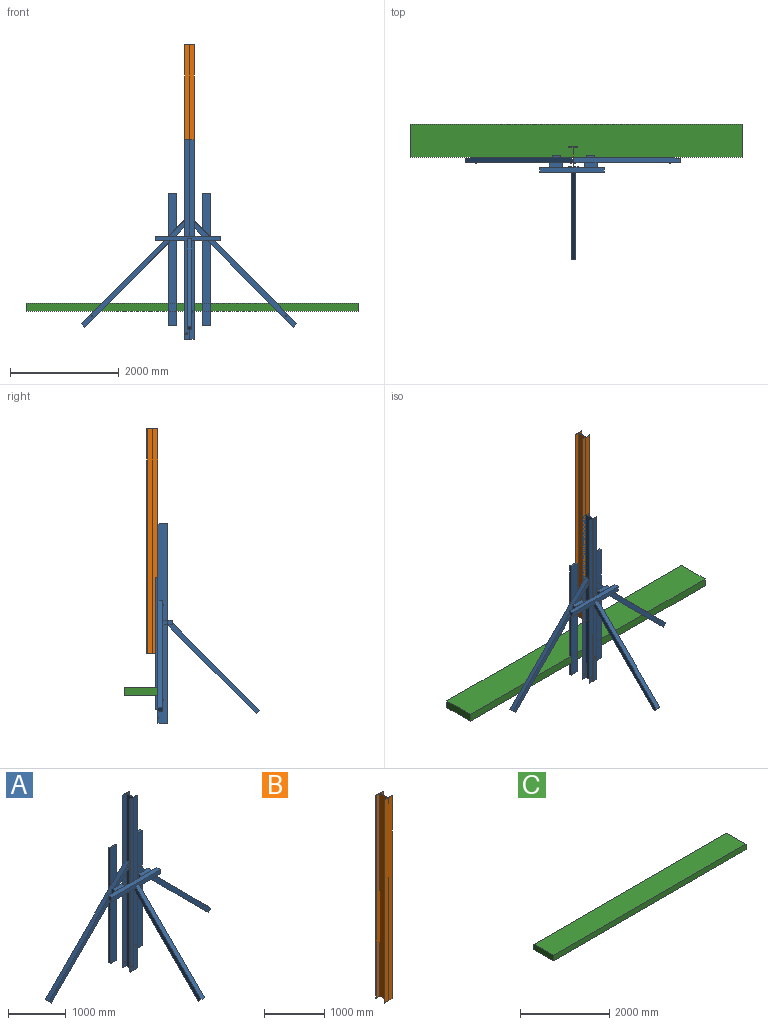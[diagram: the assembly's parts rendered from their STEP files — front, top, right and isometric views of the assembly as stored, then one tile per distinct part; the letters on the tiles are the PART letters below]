
ASSEMBLY  parts=3 mates=2
PART A: 120 faces, bbox 3962x1906.1x3657.6 mm
  f0: plane 1637.43x1605.83mm, normal (0,-1,0), area 194583.3mm2, adj f1,f43,f44,f46,f47,f48,f49,f50
  f1: plane 1915.68x1902.73mm, normal (-0.71,0,-0.7), area 239755.5mm2, adj f0,f7,f9,f11,f42,f43,f45,f80
  f2: plane 1915.68x1902.73mm, normal (0.71,0,-0.7), area 239755.5mm2, adj f3,f6,f8,f60,f61,f63,f64,f87
  f3: plane 1637.43x1617.29mm, normal (0,-1,0), area 194885.1mm2, adj f2,f61,f62,f65,f66,f67,f68,f69
  f4: plane 1766.83x174.77mm, normal (0,-1,0), area 308788mm2, adj f18,f19,f20,f102
  f5: plane 1801.87x174.77mm, normal (0,-1,0), area 313328.6mm2, adj f18,f19,f21,f22,f23,f95,f101,f103
  f6: plane 1671.48x1597.96mm, normal (0,1,0), area 197607.4mm2, adj f2,f61,f62,f88
  f7: plane 276.21x149.05mm, normal (0,1,0), area 18802.6mm2, adj f1,f13,f44,f83
  f8: plane 3657.6x81.77mm, normal (0,-1,0), area 290357mm2, adj f2,f15,f16,f20,f21,f27,f28,f29
  f9: plane 2133.6x77.79mm, normal (0,-1,0), area 162607.1mm2, adj f1,f11,f13,f21,f35,f36,f37,f38
  f10: plane 3657.6x77.79mm, normal (0,1,0), area 283723.8mm2, adj f11,f19,f20,f21,f23
  f11: plane 3657.6x167.29mm, normal (1,0,0), area 600656mm2, adj f1,f9,f10,f12,f20,f21,f42,f44
  f12: plane 1476.16x77.79mm, normal (0,-1,0), area 111781.1mm2, adj f11,f13,f20,f44
  f13: plane 3657.6x9.53mm, normal (1,0,0), area 34838.6mm2, adj f7,f9,f12,f14,f20,f21
  f14: plane 3657.6x174.77mm, normal (0,1,0), area 638983.7mm2, adj f13,f15,f20,f21,f24,f25
  f15: plane 3657.6x9.53mm, normal (-1,0,0), area 34838.6mm2, adj f8,f14,f20,f21,f60
  f16: plane 3657.6x167.29mm, normal (-1,0,0), area 611871mm2, adj f8,f17,f20,f21
  f17: plane 3657.6x81.77mm, normal (0,1,0), area 298275mm2, adj f16,f18,f20,f21,f22
  f18: plane 3657.6x9.53mm, normal (-1,0,0), area 34838.6mm2, adj f4,f5,f17,f20,f21,f98
  f19: plane 3657.6x9.53mm, normal (1,0,0), area 34838.6mm2, adj f4,f5,f10,f20,f21,f99
  f20: plane 186.34x174.77mm, normal (0,0,1), area 5874.8mm2, adj f4,f8,f10,f11,f12,f13,f14,f15
  f21: plane 186.34x174.77mm, normal (0,0,-1), area 5874.8mm2, adj f5,f8,f9,f10,f11,f13,f14,f15
  f22: cylinder r=15.88mm len=31.75mm, axis (0,-1,0), area 950.1mm2, adj f5,f17
  f23: cylinder r=15.88mm len=31.75mm, axis (0,-1,0), area 950.1mm2, adj f5,f10
  f24: cylinder r=6.35mm len=12.7mm, axis (0,-1,0), area 380mm2, adj f14,f41
  f25: cylinder r=6.35mm len=12.7mm, axis (0,-1,0), area 380mm2, adj f14,f33
  f26: plane 22x19.05mm, normal (0,-1,0), area 314.3mm2, adj f27,f28,f29,f30,f31,f32
  f27: plane 12.7x9.53mm, normal (0.87,0,-0.5), area 139.7mm2, adj f8,f26,f28,f32
  f28: plane 12.7x11mm, normal (0,0,-1), area 139.7mm2, adj f8,f26,f27,f29
  f29: plane 12.7x9.52mm, normal (-0.87,0,-0.5), area 139.7mm2, adj f8,f26,f28,f30
  f30: plane 12.7x9.53mm, normal (-0.87,0,0.5), area 139.7mm2, adj f8,f26,f29,f31
  f31: plane 12.7x11mm, normal (0,0,1), area 139.7mm2, adj f8,f26,f30,f32
  f32: plane 12.7x9.52mm, normal (0.87,0,0.5), area 139.7mm2, adj f8,f26,f27,f31
  f33: plane 12.7x12.7mm, normal (0,1,0), area 126.7mm2, adj f25
  f34: plane 21.99x19.26mm, normal (0,-1,0), area 314.3mm2, adj f35,f36,f37,f38,f39,f40
  f35: plane 12.7x9.63mm, normal (0.88,0,-0.48), area 139.7mm2, adj f9,f34,f36,f40
  f36: plane 12.7x11mm, normal (0.02,0,-1), area 139.7mm2, adj f9,f34,f35,f37
  f37: plane 12.7x9.42mm, normal (-0.86,0,-0.52), area 139.7mm2, adj f9,f34,f36,f38
  f38: plane 12.7x9.63mm, normal (-0.88,0,0.48), area 139.7mm2, adj f9,f34,f37,f39
  f39: plane 12.7x11mm, normal (-0.02,0,1), area 139.7mm2, adj f9,f34,f38,f40
  f40: plane 12.7x9.42mm, normal (0.86,0,0.52), area 139.7mm2, adj f9,f34,f35,f39
  f41: plane 12.7x12.7mm, normal (0,1,0), area 126.7mm2, adj f24
  f42: plane 367.86x365.37mm, normal (0,-1,0), area 37874.4mm2, adj f1,f11,f44,f53,f54,f55,f56,f57
  f43: plane 88.9x63.07mm, normal (0.7,0,-0.71), area 7903.2mm2, adj f0,f1,f44,f45
  f44: plane 1979.18x1965.8mm, normal (0.71,0,0.7), area 247777.3mm2, adj f0,f7,f11,f12,f42,f43,f45,f79
  f45: plane 1660.01x1586.57mm, normal (0,1,0), area 196170.3mm2, adj f1,f43,f44,f81
  f46: plane 12.7x10.63mm, normal (0.97,0,0.26), area 139.7mm2, adj f0,f47,f51,f52
  f47: plane 12.7x10.61mm, normal (0.26,0,0.97), area 139.7mm2, adj f0,f46,f48,f52
  f48: plane 12.7x7.8mm, normal (-0.7,0,0.71), area 139.7mm2, adj f0,f47,f49,f52
  f49: plane 12.7x10.63mm, normal (-0.97,0,-0.26), area 139.7mm2, adj f0,f48,f50,f52
  f50: plane 12.7x10.61mm, normal (-0.26,0,-0.97), area 139.7mm2, adj f0,f49,f51,f52
  f51: plane 12.7x7.8mm, normal (0.7,0,-0.71), area 139.7mm2, adj f0,f46,f50,f52
  f52: plane 21.27x21.23mm, normal (0,-1,0), area 314.3mm2, adj f46,f47,f48,f49,f50,f51
  f53: plane 12.7x10.63mm, normal (0.97,0,0.26), area 139.7mm2, adj f42,f54,f58,f59
  f54: plane 12.7x10.61mm, normal (0.26,0,0.97), area 139.7mm2, adj f42,f53,f55,f59
  f55: plane 12.7x7.8mm, normal (-0.7,0,0.71), area 139.7mm2, adj f42,f54,f56,f59
  f56: plane 12.7x10.63mm, normal (-0.97,0,-0.26), area 139.7mm2, adj f42,f55,f57,f59
  f57: plane 12.7x10.61mm, normal (-0.26,0,-0.97), area 139.7mm2, adj f42,f56,f58,f59
  f58: plane 12.7x7.8mm, normal (0.7,0,-0.71), area 139.7mm2, adj f42,f53,f57,f59
  f59: plane 21.27x21.23mm, normal (0,-1,0), area 314.3mm2, adj f53,f54,f55,f56,f57,f58
  f60: plane 276.06x148.89mm, normal (0,1,0), area 18783.3mm2, adj f2,f15,f62,f90
  f61: plane 88.9x63.07mm, normal (-0.7,0,-0.71), area 7903.2mm2, adj f2,f3,f6,f62
  f62: plane 1979.18x1965.8mm, normal (-0.71,0,0.7), area 247813.1mm2, adj f3,f6,f8,f60,f61,f63,f64,f86
  f63: plane 126.15x88.9mm, normal (1,0,0), area 11214.9mm2, adj f2,f8,f62,f64
  f64: plane 367.86x365.37mm, normal (0,-1,0), area 37874.4mm2, adj f2,f62,f63,f72,f73,f74,f75,f76
  f65: plane 12.7x10.63mm, normal (-0.97,0,0.26), area 139.7mm2, adj f3,f66,f70,f71
  f66: plane 12.7x10.61mm, normal (-0.26,0,0.97), area 139.7mm2, adj f3,f65,f67,f71
  f67: plane 12.7x7.8mm, normal (0.7,0,0.71), area 139.7mm2, adj f3,f66,f68,f71
  f68: plane 12.7x10.63mm, normal (0.97,0,-0.26), area 139.7mm2, adj f3,f67,f69,f71
  f69: plane 12.7x10.61mm, normal (0.26,0,-0.97), area 139.7mm2, adj f3,f68,f70,f71
  f70: plane 12.7x7.8mm, normal (-0.7,0,-0.71), area 139.7mm2, adj f3,f65,f69,f71
  f71: plane 21.27x21.23mm, normal (0,-1,0), area 314.3mm2, adj f65,f66,f67,f68,f69,f70
  f72: plane 12.7x10.63mm, normal (-0.97,0,0.26), area 139.7mm2, adj f64,f73,f77,f78
  f73: plane 12.7x10.61mm, normal (-0.26,0,0.97), area 139.7mm2, adj f64,f72,f74,f78
  f74: plane 12.7x7.8mm, normal (0.7,0,0.71), area 139.7mm2, adj f64,f73,f75,f78
  f75: plane 12.7x10.63mm, normal (0.97,0,-0.26), area 139.7mm2, adj f64,f74,f76,f78
  f76: plane 12.7x10.61mm, normal (0.26,0,-0.97), area 139.7mm2, adj f64,f75,f77,f78
  f77: plane 12.7x7.8mm, normal (-0.7,0,-0.71), area 139.7mm2, adj f64,f72,f76,f78
  f78: plane 21.27x21.23mm, normal (0,-1,0), area 314.3mm2, adj f72,f73,f74,f75,f76,f77
  f79: plane 801.76x152.4mm, normal (0,-1,0), area 110496.8mm2, adj f44,f81,f83,f85
  f80: plane 1663.92x152.4mm, normal (0,-1,0), area 241889.7mm2, adj f1,f81,f83,f84
  f81: plane 2438.4x38.1mm, normal (1,0,0), area 92903mm2, adj f45,f79,f80,f82,f84,f85
  f82: plane 2438.4x152.4mm, normal (0,1,0), area 371612.2mm2, adj f81,f83,f84,f85
  f83: plane 2438.4x38.1mm, normal (-1,0,0), area 92903mm2, adj f7,f79,f80,f82,f84,f85
  f84: plane 152.4x38.1mm, normal (0,0,-1), area 5806.4mm2, adj f80,f81,f82,f83
  f85: plane 152.4x38.1mm, normal (0,0,1), area 5806.4mm2, adj f79,f81,f82,f83
  f86: plane 790.29x152.4mm, normal (0,-1,0), area 108749mm2, adj f62,f88,f90,f92
  f87: plane 1675.39x152.4mm, normal (0,-1,0), area 243637.6mm2, adj f2,f88,f90,f91
  f88: plane 2438.4x38.1mm, normal (-1,0,0), area 92903mm2, adj f6,f86,f87,f89,f91,f92
  f89: plane 2438.4x152.4mm, normal (0,1,0), area 371612.2mm2, adj f88,f90,f91,f92
  f90: plane 2438.4x38.1mm, normal (1,0,0), area 92903mm2, adj f60,f86,f87,f89,f91,f92
  f91: plane 152.4x38.1mm, normal (0,0,-1), area 5806.4mm2, adj f87,f88,f89,f90
  f92: plane 152.4x38.1mm, normal (0,0,1), area 5806.4mm2, adj f86,f88,f89,f90
  f93: plane 1602.25x1602.25mm, normal (0,-0.71,0.71), area 201440.1mm2, adj f94,f96,f97,f100
  f94: plane 88.9x62.86mm, normal (0,-0.71,-0.71), area 7903.2mm2, adj f93,f95,f96,f97
  f95: plane 1628.28x1628.28mm, normal (0,0.71,-0.71), area 204713.7mm2, adj f5,f94,f96,f97
  f96: plane 1691.15x1665.11mm, normal (-1,0,0), area 201440.1mm2, adj f93,f94,f95,f100,f101
  f97: plane 1691.15x1665.11mm, normal (1,0,0), area 201440.1mm2, adj f93,f94,f95,f100,f103
  f98: plane 531.39x88.9mm, normal (0,1,0), area 47241mm2, adj f18,f101,f102,f105
  f99: plane 480.02x88.9mm, normal (0,1,0), area 42673.4mm2, adj f19,f102,f103,f104
  f100: plane 1186.18x88.9mm, normal (0,-1,0), area 102177.8mm2, adj f93,f96,f97,f101,f102,f103,f104,f105
  f101: plane 576.58x88.9mm, normal (0,0,-1), area 51258mm2, adj f5,f96,f98,f100,f105
  f102: plane 1186.18x88.9mm, normal (0,0,1), area 105451.4mm2, adj f4,f98,f99,f100,f104,f105
  f103: plane 520.7x88.9mm, normal (0,0,-1), area 46290.2mm2, adj f5,f97,f99,f100,f104
  f104: plane 88.9x88.9mm, normal (1,0,0), area 7903.2mm2, adj f99,f100,f102,f103
  f105: plane 88.9x88.9mm, normal (-1,0,0), area 7903.2mm2, adj f98,f100,f101,f102
  f106: plane 142.93x88.9mm, normal (0,1,0), area 8781.2mm2, adj f2,f107,f109,f111
  f107: plane 236.22x88.9mm, normal (0,0,-1), area 20793.3mm2, adj f2,f3,f106,f108,f111,f112
  f108: plane 236.22x88.9mm, normal (0,-1,0), area 21000mm2, adj f107,f109,f111,f112
  f109: plane 236.22x88.9mm, normal (0,0,1), area 20722.4mm2, adj f2,f62,f64,f106,f108,f110,f111,f112
  f110: plane 56.68x56.29mm, normal (0,1,0), area 1595.3mm2, adj f62,f109,f112
  f111: plane 88.9x88.9mm, normal (1,0,0), area 7903.2mm2, adj f106,f107,f108,f109
  f112: plane 88.9x88.9mm, normal (-1,0,0), area 7831.8mm2, adj f3,f62,f107,f108,f109,f110
  f113: plane 131.53x88.9mm, normal (0,1,0), area 7768.4mm2, adj f1,f114,f116,f118
  f114: plane 236.22x88.9mm, normal (0,0,-1), area 20768.1mm2, adj f0,f1,f113,f115,f118,f119
  f115: plane 236.22x88.9mm, normal (0,-1,0), area 21000mm2, adj f114,f116,f118,f119
  f116: plane 236.22x88.9mm, normal (0,0,1), area 20722.4mm2, adj f1,f42,f44,f113,f115,f117,f118,f119
  f117: plane 68.15x67.69mm, normal (0,1,0), area 2306.3mm2, adj f44,f116,f119
  f118: plane 88.9x88.9mm, normal (-1,0,0), area 7903.2mm2, adj f113,f114,f115,f116
  f119: plane 88.9x88.9mm, normal (1,0,0), area 7857.2mm2, adj f0,f44,f114,f115,f116,f117
PART B: 16 faces, bbox 174.8x203.2x4127.5 mm
  f0: plane 4127.5x174.77mm, normal (0,-1,0), area 721361.2mm2, adj f1,f13,f14,f15
  f1: plane 4127.5x9.53mm, normal (1,0,0), area 39314.4mm2, adj f0,f2,f14,f15
  f2: plane 4127.5x83.47mm, normal (0,1,0), area 344505.9mm2, adj f1,f3,f14,f15
  f3: plane 4127.5x92.08mm, normal (1,0,0), area 380039.6mm2, adj f2,f4,f14,f15
  f4: plane 4127.5x0.01mm, normal (0,1,0), area 52.4mm2, adj f3,f5,f14,f15
  f5: plane 4127.5x92.08mm, normal (1,0,0), area 380039.6mm2, adj f4,f6,f14,f15
  f6: plane 4127.5x77.79mm, normal (0,-1,0), area 321067.9mm2, adj f5,f7,f14,f15
  f7: plane 4127.5x9.53mm, normal (1,0,0), area 39314.4mm2, adj f6,f8,f14,f15
  f8: plane 4127.5x169.08mm, normal (0,1,0), area 697870.8mm2, adj f7,f9,f14,f15
  f9: plane 4127.5x9.53mm, normal (-1,0,0), area 39314.4mm2, adj f8,f10,f14,f15
  f10: plane 4127.5x81.77mm, normal (0,-1,0), area 337488.4mm2, adj f9,f11,f14,f15
  f11: plane 4127.5x184.15mm, normal (-1,0,0), area 760079.1mm2, adj f10,f12,f14,f15
  f12: plane 4127.5x81.77mm, normal (0,1,0), area 337488.4mm2, adj f11,f13,f14,f15
  f13: plane 4127.5x9.53mm, normal (-1,0,0), area 39314.4mm2, adj f0,f12,f14,f15
  f14: plane 203.2x174.77mm, normal (0,0,1), area 5030.3mm2, adj f0,f1,f2,f3,f4,f5,f6,f7
  f15: plane 203.2x174.77mm, normal (0,0,-1), area 5030.3mm2, adj f0,f1,f2,f3,f4,f5,f6,f7
PART C: 6 faces, bbox 6096x609.6x152.4 mm
  f0: plane 609.6x152.4mm, normal (1,0,0), area 92903mm2, adj f1,f3,f4,f5
  f1: plane 6096x609.6mm, normal (0,0,-1), area 3716121.6mm2, adj f0,f2,f4,f5
  f2: plane 609.6x152.4mm, normal (-1,0,0), area 92903mm2, adj f1,f3,f4,f5
  f3: plane 6096x609.6mm, normal (0,0,1), area 3716121.6mm2, adj f0,f2,f4,f5
  f4: plane 6096x152.4mm, normal (0,1,0), area 929030.4mm2, adj f0,f1,f2,f3
  f5: plane 6096x152.4mm, normal (0,-1,0), area 929030.4mm2, adj f0,f1,f2,f3
PLACE A t=(-49.99,120.65,25.4)mm
PLACE B t=(-50.14,92.08,690.59)mm
PLACE C t=(0,-111.9,76.2)mm
MATE slider A.f20 <-> B.f14  axis (0,0,-1) through (38.1,-9.53,3073.4)mm
MATE fastened A.f23 <-> C.f5  axis (0,1,0) through (0,0,-76.2)mm
